# Revit family: QF_BPRO_SW 10x6 - 3 Basic_573488
name_source: partatom
category: Sonderausstattung
revit_build: Autodesk Revit 2018 (Build: 20190510_1515(x64)
units: mm (PartAtom-declared; Revit-internal decimal feet)

## family parameters
Arbeitsebenenbasiert = Nein
Beim Laden mit Abzugskörper schneiden = Nein
Bemaßung runder Anschluss = Durchmesser verwenden
Gemeinsam genutzt = Nein
Immer vertikal = Ja
Raumberechnungspunkt = Nein
Teiletyp = Normal

## types (1)
- SW 10x6 - 3 Basic
    Artikel Nummer = 573488
    Beschreibung = Servierwagen aus rostfreiem Edelstahl
mit 3 Borden 1000 x 600 mm
max. Belastung je Bord: 80 kg
Tragfähigkeit: 120 kg
    Beschreibung durch Hersteller analog Leistungsverzeichniskurztext = Abmessungen

Länge:			1100 mm
Breite:			  700 mm
Höhe:			  950 mm

Lichtes Maß:
Höhe zwischen den Borden:	  275 mm
Borde:		   	1000 x 600 mm


Ausführung

Servierwagen SW 10x6 in Basisausführung.
Der Servierwagen besteht aus CNS 18/10, Werkstoff-Nr. 1.4301. Zwischen stabilem Rundrohr mit D = 25 mm befinden sich drei eingeschweißte tiefgezogene Borde. Die Oberfläche der Borde ist mikroliert. Die Rundrohre an den Stirnseiten werden als Schiebegriffe genutzt. Ein umlaufender 35 mm abgekanteter Profilrand an den Borden, die Rollierung der Bordkante sowie durchgehende Schweißnähte zwischen Rohrrahmen und Borden verstärken die Stabilität des Servierwagens. 
Die Borde sind mit einer schalldämmenden Antidröhnmatte unterfüttert.

Der Servierwagen ist fahrbar mittels rostfreien Kunststoffrollen gemäß DIN 18867, Teil 8 (4 Lenkrollen, davon 2 mit Feststeller, Rollendurchmesser 125 mm). Die Rollen sind im Rohrrahmen eingesteckt. Wandabweiser aus Kunststoff (Polyethylen) an allen vier Ecken schützen vor Beschädigung.

Zubehör/ Optionen

•	Besteckaufsatz CAT 5 aus CNS inkl. 5 Besteckbehälter GN 1/4-150 mit transparenter, halbseitig klappbarer Plexiglas-Abdeckung, 500 Besteckteile. Zur einfachen Montage auf den Rohrbügeln (Best.Nr. 574 772)
•	Abfallbehälter AFB 4 x 2 x 2,5 aus CNS, mit Hängevorrichtung, 18,5 Liter (Best.Nr. 555 509)
•	Besteckbehälter BGN 1/3-150 aus CNS, mit Hängevorrichtung, 110 Besteckteile (Best.Nr. 555 510)
•	Galerie umlaufend, 50 mm hoch 
•	Knotenbleche zur Stärkung der Stabiliät
•	Bordverstärkungsprofile (Wenn Bordverstärkungsprofil, keine Antidröhnmatte enthalten) 
•	Luftidentische Rollen, 4 Lenkrollen, davon 2 mit Feststeller, Durchmesser 125 mm

Verkleidungs-Sets:

•	Verkleidung 3-seitig aus Edelstahl, zum Einhängen an Servierwagen, Best.Nr.: 375451
•	Verkleidung 3-seitig mit frontseitigen Flügeltüren aus Edelstahl, zur einfachen Montage an Servierwagen, Best.Nr.: 375452 (nicht möglich in Kombination mit Knotenblechen)
•	Verkleidung 3-seitig aus Feinblech, doppelseitig elektrolytisch verzinkt, pulverbeschichtet in verschiedenen Farben, zum Einhängen an Servierwagen, Best.Nr.: 375455
•	Verkleidung 3-seitig mit frontseitigen Flügeltüren aus Feinblech, doppelseitig elektrolytisch verzinkt, pulverbeschichtet in verschiedenen Farben, zur einfachen Montage an Servierwagen, Best.Nr.: 375456 (nicht möglich in Kombination mit Knotenblechen)


Technische Daten

Werkstoff:	Chromnickelstahl 18/10,
		Polyamid (PA)
Gewicht:		20,8 kg
Tragfähigkeit je Wagen:	120 kg
Tragfähigkeit je Bord:	 80 kg
Anzahl der Borde:		    3


Besonderheit

•	Umlaufender Profilrand an den Borden zur Verstärkung der Stabilität des Servierwagens und Verhinderung von seitlichem Abrutschen der abgestellten Gegenstände

•	Rollierung der Bordkante: eingerollte Kanten sorgen für hohe Stabilität und schützen das Personal vor Verletzungen.


Fabrikat

Hersteller:	B.PRO
Typ:                                      SW 10x6-3 BASIC
Best.Nr.		573488
    Beschreibung durch Hersteller analog Leistungsverzeichnislangtext = Abmessungen

Länge:			1100 mm
Breite:			  700 mm
Höhe:			  950 mm

Lichtes Maß:
Höhe zwischen den Borden:	  275 mm
Borde:		   	1000 x 600 mm


Ausführung

Servierwagen SW 10x6 in Basisausführung.
Der Servierwagen besteht aus CNS 18/10, Werkstoff-Nr. 1.4301. Zwischen stabilem Rundrohr mit D = 25 mm befinden sich drei eingeschweißte tiefgezogene Borde. Die Oberfläche der Borde ist mikroliert. Die Rundrohre an den Stirnseiten werden als Schiebegriffe genutzt. Ein umlaufender 35 mm abgekanteter Profilrand an den Borden, die Rollierung der Bordkante sowie durchgehende Schweißnähte zwischen Rohrrahmen und Borden verstärken die Stabilität des Servierwagens. 
Die Borde sind mit einer schalldämmenden Antidröhnmatte unterfüttert.

Der Servierwagen ist fahrbar mittels rostfreien Kunststoffrollen gemäß DIN 18867, Teil 8 (4 Lenkrollen, davon 2 mit Feststeller, Rollendurchmesser 125 mm). Die Rollen sind im Rohrrahmen eingesteckt. Wandabweiser aus Kunststoff (Polyethylen) an allen vier Ecken schützen vor Beschädigung.

Zubehör/ Optionen

•	Besteckaufsatz CAT 5 aus CNS inkl. 5 Besteckbehälter GN 1/4-150 mit transparenter, halbseitig klappbarer Plexiglas-Abdeckung, 500 Besteckteile. Zur einfachen Montage auf den Rohrbügeln (Best.Nr. 574 772)
•	Abfallbehälter AFB 4 x 2 x 2,5 aus CNS, mit Hängevorrichtung, 18,5 Liter (Best.Nr. 555 509)
•	Besteckbehälter BGN 1/3-150 aus CNS, mit Hängevorrichtung, 110 Besteckteile (Best.Nr. 555 510)
•	Galerie umlaufend, 50 mm hoch 
•	Knotenbleche zur Stärkung der Stabiliät
•	Bordverstärkungsprofile (Wenn Bordverstärkungsprofil, keine Antidröhnmatte enthalten) 
•	Luftidentische Rollen, 4 Lenkrollen, davon 2 mit Feststeller, Durchmesser 125 mm

Verkleidungs-Sets:

•	Verkleidung 3-seitig aus Edelstahl, zum Einhängen an Servierwagen, Best.Nr.: 375451
•	Verkleidung 3-seitig mit frontseitigen Flügeltüren aus Edelstahl, zur einfachen Montage an Servierwagen, Best.Nr.: 375452 (nicht möglich in Kombination mit Knotenblechen)
•	Verkleidung 3-seitig aus Feinblech, doppelseitig elektrolytisch verzinkt, pulverbeschichtet in verschiedenen Farben, zum Einhängen an Servierwagen, Best.Nr.: 375455
•	Verkleidung 3-seitig mit frontseitigen Flügeltüren aus Feinblech, doppelseitig elektrolytisch verzinkt, pulverbeschichtet in verschiedenen Farben, zur einfachen Montage an Servierwagen, Best.Nr.: 375456 (nicht möglich in Kombination mit Knotenblechen)


Technische Daten

Werkstoff:	Chromnickelstahl 18/10,
		Polyamid (PA)
Gewicht:		20,8 kg
Tragfähigkeit je Wagen:	120 kg
Tragfähigkeit je Bord:	 80 kg
Anzahl der Borde:		    3


Besonderheit

•	Umlaufender Profilrand an den Borden zur Verstärkung der Stabilität des Servierwagens und Verhinderung von seitlichem Abrutschen der abgestellten Gegenstände

•	Rollierung der Bordkante: eingerollte Kanten sorgen für hohe Stabilität und schützen das Personal vor Verletzungen.


Fabrikat

Hersteller:	B.PRO
Typ:                                      SW 10x6-3 BASIC
Best.Nr.		573488
    Breite Korpus = 600 mm  [stored 1.9685 ft]
    Gerätegewicht Netto = 20.80 kg
    Großküchengerätezuordnung = Ja
    Hersteller = B.PRO GmbH
    Höhe = 950 mm
    Höhe2 = 938 mm
    Internetadresse Gerätehersteller = https://www.bpro-solutions.com
    Internetadresse für Ersatzteilliste = https://www.bpro-solutions.com
    Kosten = 654.2 $
    Länge Gerätebreite = 1100 mm
    Länge Korpus = 1000 mm  [stored 3.28084 ft]
    Material = QF_Metal-Stainless-Steel_general
    Material_Stoßschutz = QF_Rubber-Black-Matt
    Modell = SW 10 x 6-3 BASIC
    Sockelhöhe = 180 mm  [stored 0.590551 ft]
    Tiefe = 700 mm
    Typenkommentare = Servierwagen 10 x 6-3 BASIC
    URL = https://www.bpro-solutions.com
    Warnhinweise = Ausführliche Gefahrenhinweise entnehmen Sie der Betriebsanleitung.
    Zubehör = Nein

note: [stored X ft] marks values corroborated as IEEE doubles in the binary element streams (Revit-internal decimal feet)
